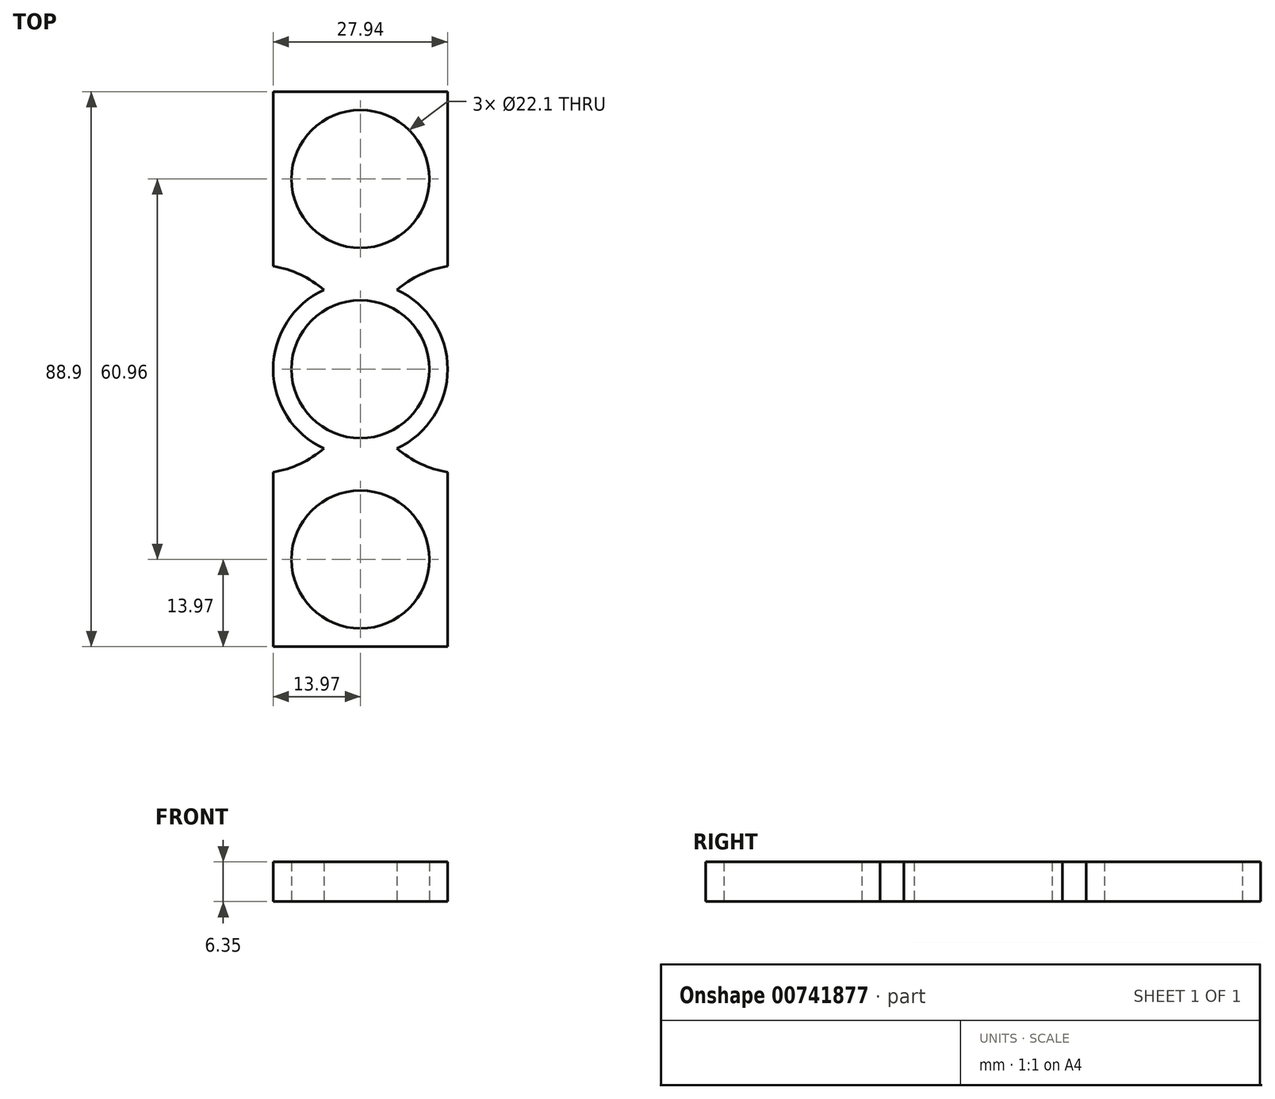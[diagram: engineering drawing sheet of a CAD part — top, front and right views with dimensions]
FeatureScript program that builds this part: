
annotation { "Feature Type Name" : "Feature", "Feature Type Description" : "" }
export const myFeature = defineFeature(function(context is Context, id is Id, definition is map)
    precondition{}
    {
        {
            var Q0;
            Q0=qCreatedBy(makeId("Top.planeOp"),FACE);
            var sketch = newSketch(context, id + "F0", { "sketchPlane" : qUnion([Q0])});
            skCircle(sketch, "E0", {"center": v(0, 0) * mm, "radius": 13.97 * mm});
            skCircle(sketch, "E1", {"center": v(0, 0) * mm, "radius": 11.05 * mm});
            skLineSegment(sketch, "E2", {"start": v(0, 0) * mm, "end": v(0, 30.48) * mm});
            skCircle(sketch, "E3", {"center": v(0, 30.48) * mm, "radius": 13.97 * mm});
            skCircle(sketch, "E4", {"center": v(0, 30.48) * mm, "radius": 11.05 * mm});
            skLineSegment(sketch, "E5", {"start": v(0, 0) * mm, "end": v(0, -30.48) * mm});
            skCircle(sketch, "E6", {"center": v(0, -30.48) * mm, "radius": 11.05 * mm});
            skCircle(sketch, "E7", {"center": v(0, -30.48) * mm, "radius": 13.97 * mm});
            skCircle(sketch, "E8.cCircle", {"center": v(0, -30.48) * mm, "radius": 13.97 * mm, "construction": true});
            skLineSegment(sketch, "E8.0", {"start": v(13.97, -16.5) * mm, "end": v(13.97, -44.45) * mm});
            skLineSegment(sketch, "E8.1", {"start": v(13.97, -44.45) * mm, "end": v(-13.97, -44.45) * mm});
            skLineSegment(sketch, "E8.2", {"start": v(-13.97, -44.45) * mm, "end": v(-13.97, -16.5) * mm});
            skLineSegment(sketch, "E8.3", {"start": v(-13.97, -16.5) * mm, "end": v(13.97, -16.5) * mm});
            skPoint(sketch, "E8.0.midPoint", {"position": v(13.97, -30.48) * mm});
            skCircle(sketch, "E9.cCircle", {"center": v(0, 30.48) * mm, "radius": 13.97 * mm, "construction": true});
            skLineSegment(sketch, "E9.0", {"start": v(13.97, 44.45) * mm, "end": v(13.97, 16.5) * mm});
            skLineSegment(sketch, "E9.1", {"start": v(13.97, 16.5) * mm, "end": v(-13.97, 16.5) * mm});
            skLineSegment(sketch, "E9.2", {"start": v(-13.97, 16.5) * mm, "end": v(-13.97, 44.45) * mm});
            skLineSegment(sketch, "E9.3", {"start": v(-13.97, 44.45) * mm, "end": v(13.97, 44.45) * mm});
            skPoint(sketch, "E9.0.midPoint", {"position": v(13.97, 30.48) * mm});
            skPoint(sketch, "E10", {"position": v(-13.97, 30.48) * mm});
            skArc(sketch, "E11", {"start": v(-13.97, -16.5) * mm, "mid": v(-9.64, -15.16) * mm, "end": v(-5.83, -12.7) * mm});
            skArc(sketch, "E12", {"start": v(13.97, 16.5) * mm, "mid": v(9.64, 15.16) * mm, "end": v(5.83, 12.7) * mm});
            skArc(sketch, "E13.trimOffspring", {"start": v(-5.83, 12.7) * mm, "mid": v(-9.64, 15.16) * mm, "end": v(-13.97, 16.5) * mm});
            skArc(sketch, "E14.trimOffspring", {"start": v(5.84, -12.69) * mm, "mid": v(9.65, -15.15) * mm, "end": v(13.97, -16.51) * mm});
            skSolve(sketch);
        }
        {
            var Q0;
            Q0 = qSketchRegion(id + "F0", true);
            extrude(context, id + "F1", {"entities" : qUnion([Q0]), "depth" : 6.35 * mm, "offsetDistance" : 25.4 * mm});
        }
    });
